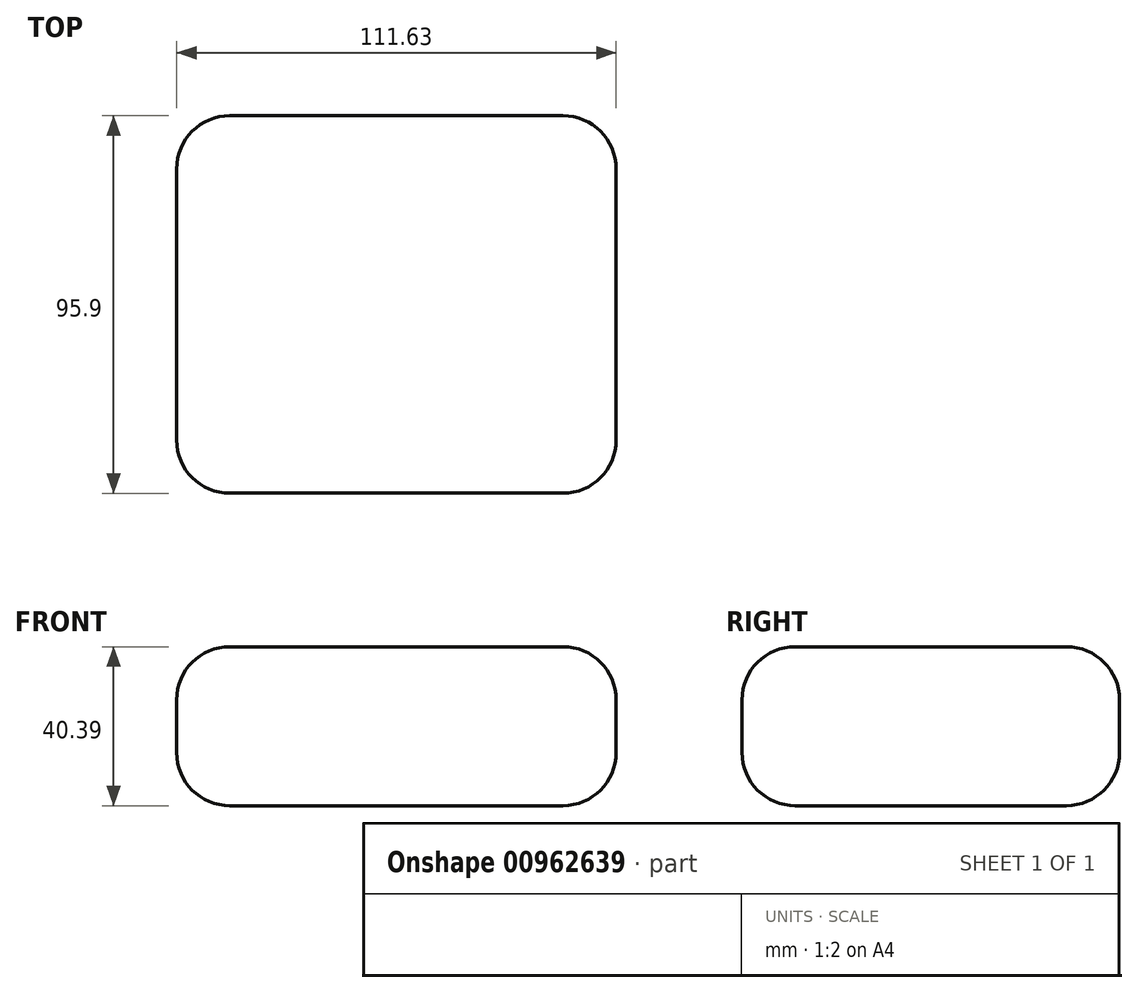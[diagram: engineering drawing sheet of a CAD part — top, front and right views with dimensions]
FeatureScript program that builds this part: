
annotation { "Feature Type Name" : "Feature", "Feature Type Description" : "" }
export const myFeature = defineFeature(function(context is Context, id is Id, definition is map)
    precondition{}
    {
        {
            var Q0;
            Q0=qCreatedBy(makeId("Top.planeOp"),FACE);
            var sketch = newSketch(context, id + "F0", { "sketchPlane" : qUnion([Q0])});
            skLineSegment(sketch, "E0.bottom", {"start": v(-54.15, -43.18) * mm, "end": v(57.48, -43.18) * mm});
            skLineSegment(sketch, "E0.top", {"start": v(-54.15, 52.72) * mm, "end": v(57.48, 52.72) * mm});
            skLineSegment(sketch, "E0.left", {"start": v(-54.15, -43.18) * mm, "end": v(-54.15, 52.72) * mm});
            skLineSegment(sketch, "E0.right", {"start": v(57.48, -43.18) * mm, "end": v(57.48, 52.72) * mm});
            skSolve(sketch);
        }
        {
            var Q0;
            Q0=makeQuery(id+"F0.imprint","IMPRINT",FACE,{"disambiguationData":[TD([[makeQuery(id+"F0.imprint","IMPRINT",EDGE,{"derivedFrom":sQuery(id+"F0.wireOp",EDGE,"E0.bottom")}),1.0]])]});
            extrude(context, id + "F1", {"entities" : qUnion([Q0]), "depth" : 40.4 * mm, "offsetDistance" : 25.4 * mm});
        }
        {
            var Q0;
            Q0=makeQuery(id+"F1.opExtrude","SWEPT_FACE",FACE,{"disambiguationData":[OSD([sQuery(id+"F0.wireOp",EDGE,"E0.right")])]});
            var Q1;
            Q1=makeQuery(id+"F1.opExtrude","CAP_EDGE",EDGE,{"disambiguationData":[OSD([sQuery(id+"F0.wireOp",EDGE,"E0.bottom")])],"isStart":false});
            var Q2;
            Q2=makeQuery(id+"F1.opExtrude","CAP_EDGE",EDGE,{"disambiguationData":[OSD([sQuery(id+"F0.wireOp",EDGE,"E0.top")])],"isStart":false});
            var Q3;
            Q3=makeQuery(id+"F1.opExtrude","CAP_EDGE",EDGE,{"disambiguationData":[OSD([sQuery(id+"F0.wireOp",EDGE,"E0.bottom")])],"isStart":true});
            var Q4;
            Q4=makeQuery(id+"F1.opExtrude","SWEPT_EDGE",EDGE,{"disambiguationData":[OSD([sQuery(id+"F0.wireOp",EDGE,"E0.bottom"),sQuery(id+"F0.wireOp",EDGE,"E0.left")])]});
            var Q5;
            Q5=makeQuery(id+"F1.opExtrude","CAP_EDGE",EDGE,{"disambiguationData":[OSD([sQuery(id+"F0.wireOp",EDGE,"E0.top")])],"isStart":true});
            var Q6;
            Q6=makeQuery(id+"F1.opExtrude","SWEPT_EDGE",EDGE,{"disambiguationData":[OSD([sQuery(id+"F0.wireOp",EDGE,"E0.top"),sQuery(id+"F0.wireOp",EDGE,"E0.left")])]});
            var Q7;
            Q7=makeQuery(id+"F1.opExtrude","CAP_EDGE",EDGE,{"disambiguationData":[OSD([sQuery(id+"F0.wireOp",EDGE,"E0.left")])],"isStart":true});
            var Q8;
            Q8=makeQuery(id+"F1.opExtrude","CAP_EDGE",EDGE,{"disambiguationData":[OSD([sQuery(id+"F0.wireOp",EDGE,"E0.left")])],"isStart":false});
            fillet(context, id + "F2", {"entities" : qUnion([Q0, Q1, Q2, Q3, Q4, Q5, Q6, Q7, Q8]), "radius" : 13.5 * mm, "tangentPropagation" : true, "allowEdgeOverflow" : false});
        }
    });
